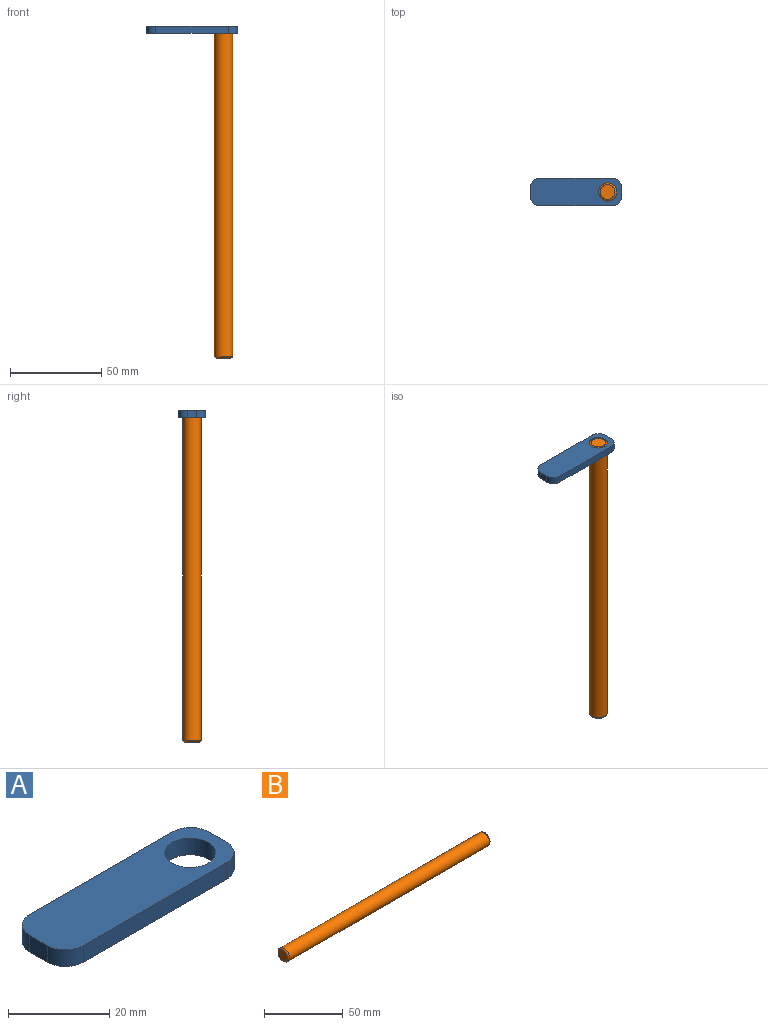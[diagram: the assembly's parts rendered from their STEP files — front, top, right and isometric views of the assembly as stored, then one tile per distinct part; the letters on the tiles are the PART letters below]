
ASSEMBLY  parts=2 mates=1
PART A: 11 faces, bbox 50x15x4 mm
  f0: plane 5x4mm, normal (-1,0,0), area 20mm2, adj f5,f6,f8,f9
  f1: plane 40x4mm, normal (0,1,0), area 160mm2, adj f5,f6,f9,f10
  f2: plane 5x4mm, normal (1,0,0), area 20mm2, adj f5,f6,f7,f10
  f3: cylinder r=5mm len=10mm, axis (0,0,-1), area 125.7mm2, adj f5,f6
  f4: plane 40x4mm, normal (0,-1,0), area 160mm2, adj f5,f6,f7,f8
  f5: plane 50x15mm, normal (0,0,-1), area 650mm2, adj f0,f1,f2,f3,f4,f7,f8,f9
  f6: plane 50x15mm, normal (0,0,1), area 650mm2, adj f0,f1,f2,f3,f4,f7,f8,f9
  f7: cylinder r=5mm len=5mm, axis (0,0,-1), area 31.4mm2, adj f2,f4,f5,f6
  f8: cylinder r=5mm len=5mm, axis (0,0,1), area 31.4mm2, adj f0,f4,f5,f6
  f9: cylinder r=5mm len=5mm, axis (0,0,-1), area 31.4mm2, adj f0,f1,f5,f6
  f10: cylinder r=5mm len=5mm, axis (0,0,1), area 31.4mm2, adj f1,f2,f5,f6
PART B: 5 faces, bbox 182x10.8x10.8 mm
  f0: cylinder r=5mm len=180mm, axis (-1,0,0), area 5654.9mm2, adj f3,f4
  f1: plane 8x8mm, normal (1,0,0), area 50.3mm2, adj f4
  f2: plane 8x8mm, normal (-1,0,0), area 50.3mm2, adj f3
  f3: torus R=4mm, axis (1,0,0), area 45.8mm2, adj f0,f2
  f4: torus R=4mm, axis (1,0,0), area 45.8mm2, adj f0,f1
PLACE A t=(27.35,0.86,-30.8)mm
PLACE B rot(axis=(0.71,0,-0.71),180deg) t=(69.67,8.36,-30.8)mm
MATE fastened B.f0 <-> A.f3  axis (0,0,1) through (69.67,8.36,-30.8)mm
